# Revit family: RN 26040 Rubinetto a sfera a 3 componenti con flange
name_source: partatom
category: Rohrzubehör
units: mm (PartAtom-declared; Revit-internal decimal feet)

## family parameters
Arbeitsebenenbasiert = Nein
Beim Laden mit Abzugskörper schneiden = Nein
Bemaßung runder Anschluss = Durchmesser verwenden
Gemeinsam genutzt = Nein
Immer vertikal = Ja
Teiletyp = Ventil - Zerlegung in

## types (5) — shared parameters
1.010.00.2 Number of the part of the guideline = 2
1.010.00.3 Issue date (month) of the guideline = 201601
1.010.00.4 Manufacturer name = R. Nussbaum AG
1.010.00.5 Revision date of the file = 20190514
1.100.00.3 Sort number for display sequence = 4
1.100.00.4 Product designation = Absperr- und Regelarmaturen
1.960/3L.00.8 Link (URL) = https://www.nussbaum.ch
2.700.00.4 valve assembly type = 11
2.700.00.7 maximum operating temperature TB [°C] = 100
2.700.00.8 maximum operating pressure(working pressure) ps [1.0 · 102 Pa] = 16
Connector Visibility = Nein
EnclosingSpace Visibility = Nein
Hersteller = R. Nussbauzm AG
Modell = 0
URL = https://www.nussbaum.ch

## per-type parameters (varying)
| type | 1.800.00.3 BS number | 1.810.00.3 Manufacturer’s reference number | 1.810.00.4 DATANORM number | 1.810.00.5 StLB number | 1.810.00.6 GTIN number | 2.700.00.26 product description | 2.700.00.5 nominal size DN | 2.700.00.6 kvs-value [m3/h] | CONNECTOR0_DIAMETER_dX_0r | CONNECTOR0_dX_00 | CONNECTOR0_dX_01 | CONNECTOR0_ref_dX | CONNECTOR1_DIAMETER_dX_0r | CONNECTOR1_dX_00 | CONNECTOR1_dX_01 | CONNECTOR1_ref_dX | R. Nussbaum AG 26040.58 en Visibility | R. Nussbaum AG 26040.59 en Visibility | R. Nussbaum AG 26040.60 en Visibility | R. Nussbaum AG 26040.61 en Visibility | R. Nussbaum AG 26040.62 en Visibility | Typenkommentare |
| DN 40 | 00401800000000000000000000000900700000000000000003???00000 | 26040.58 | 26040.58 | 728.115 | 7612945704467 | 26040.58, Kugelhahn 3-teilig mit Flanschen, Edelstahl, DN=40 | 40 | 160 | 40 mm | 101 mm | 100 mm  [stored 0.328084 ft] | 101 mm | 40 mm | 100 mm  [stored 0.328084 ft] | 101 mm | 101 mm | Ja | Nein | Nein | Nein | Nein | Valvola d'arrestoDN 40 |
| DN 50 | 00401800000000000000000000000900700000000000000004???00000 | 26040.59 | 26040.59 | 728.116 | 7612945704474 | 26040.59, Kugelhahn 3-teilig mit Flanschen, Edelstahl, DN=50 | 50 | 230 | 50 mm | 116 mm | 115 mm | 116 mm | 50 mm | 115 mm | 116 mm | 116 mm | Nein | Ja | Nein | Nein | Nein | Valvola d'arrestoDN 50 |
| DN 65 | 00401800000000000000000000000900700000000000000005???00000 | 26040.60 | 26040.60 | 728.117 | 7612945704481 | 26040.60, Kugelhahn 3-teilig mit Flanschen, Edelstahl, DN=65 | 65 | 510 | 65 mm | 146 mm | 145 mm | 146 mm | 65 mm | 145 mm | 146 mm | 146 mm | Nein | Nein | Ja | Nein | Nein | Valvola d'arrestoDN 65 |
| DN 80 | 00401800000000000000000000000900700000000000000006???00000 | 26040.61 | 26040.61 | 728.118 | 7612945704498 | 26040.61, Kugelhahn 3-teilig mit Flanschen, Edelstahl, DN=80 | 80 | 797 | 80 mm | 156 mm | 155 mm | 156 mm | 80 mm | 155 mm | 156 mm | 156 mm | Nein | Nein | Nein | Ja | Nein | Valvola d'arrestoDN 80 |
| DN 100 | 00401800000000000000000000000900700000000000000007???00000 | 26040.62 | 26040.62 | 728.121 | 7612945704504 | 26040.62, Kugelhahn 3-teilig mit Flanschen, Edelstahl, DN=100 | 100 | 1297 | 100 mm  [stored 0.328084 ft] | 176 mm | 175 mm  [stored 0.574147 ft] | 176 mm | 100 mm  [stored 0.328084 ft] | 175 mm  [stored 0.574147 ft] | 176 mm | 176 mm | Nein | Nein | Nein | Nein | Ja | Valvola d'arrestoDN 100 |

note: [stored X ft] marks values corroborated as IEEE doubles in the binary element streams (Revit-internal decimal feet)

## geometry (parser evidence)
native form markers: Sweep x1
no freeform markers — native parametric forms only
